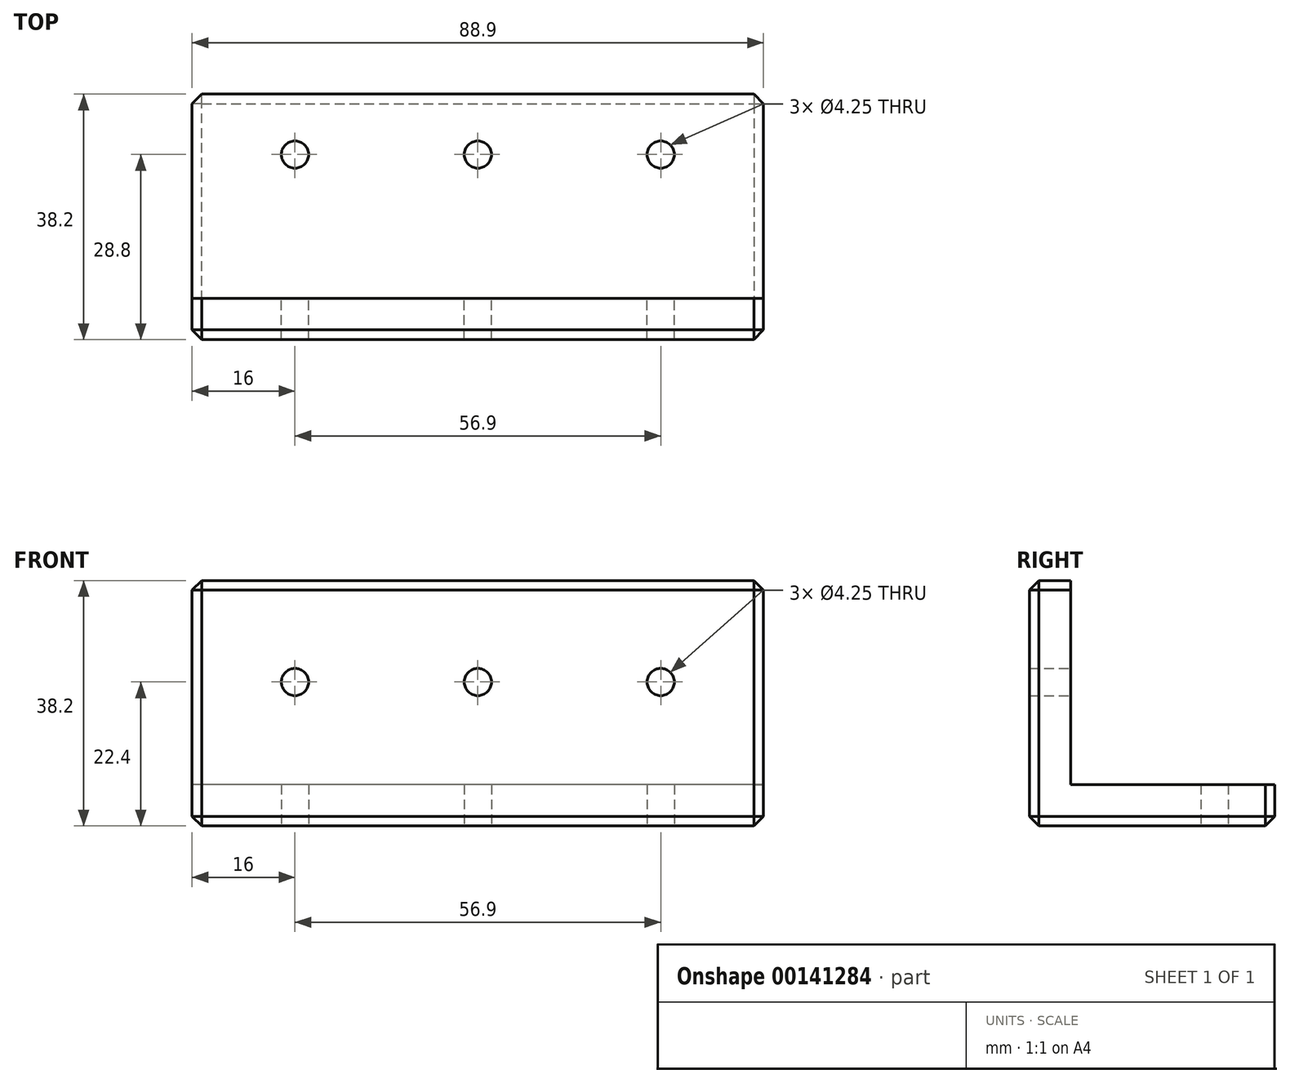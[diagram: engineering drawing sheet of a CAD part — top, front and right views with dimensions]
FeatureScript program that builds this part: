
annotation { "Feature Type Name" : "Feature", "Feature Type Description" : "" }
export const myFeature = defineFeature(function(context is Context, id is Id, definition is map)
    precondition{}
    {
        {
            var Q0;
            Q0=qCreatedBy(makeId("Top.planeOp"),FACE);
            var sketch = newSketch(context, id + "F0", { "sketchPlane" : qUnion([Q0])});
            skLineSegment(sketch, "E0.bottom", {"start": v(44.45, -15.9) * mm, "end": v(-44.45, -15.9) * mm});
            skLineSegment(sketch, "E0.top", {"start": v(44.45, 15.9) * mm, "end": v(-44.45, 15.9) * mm});
            skLineSegment(sketch, "E0.left", {"start": v(44.45, -15.9) * mm, "end": v(44.45, 15.9) * mm});
            skLineSegment(sketch, "E0.right", {"start": v(-44.45, -15.9) * mm, "end": v(-44.45, 15.9) * mm});
            skPoint(sketch, "E0.middle", {"position": v(0, 0) * mm});
            skLineSegment(sketch, "E1", {"start": v(-44.45, -9.5) * mm, "end": v(44.45, -9.5) * mm, "construction": true});
            skCircle(sketch, "E2", {"center": v(0, 6.5) * mm, "radius": 2.12 * mm});
            skCircle(sketch, "E3", {"center": v(-28.45, 6.5) * mm, "radius": 2.12 * mm});
            skCircle(sketch, "E4.MirrorC", {"center": v(28.45, 6.5) * mm, "radius": 2.12 * mm});
            skSolve(sketch);
        }
        {
            var Q0;
            Q0=qSketchRegion(id+"F0",true);
            extrude(context, id + "F1", {"entities" : qUnion([Q0]), "depth" : 6.4 * mm});
        }
        {
            var Q0;
            Q0=makeQuery(id+"F1.opExtrude","SWEPT_FACE",FACE,{"disambiguationData":[OSD([sQuery(id+"F0.wireOp",EDGE,"E0.bottom")])]});
            var sketch = newSketch(context, id + "F2", { "sketchPlane" : qUnion([Q0])});
            skLineSegment(sketch, "E5.bottom", {"start": v(-44.45, 38.2) * mm, "end": v(44.45, 38.2) * mm});
            skLineSegment(sketch, "E5.top", {"start": v(-44.45, 0) * mm, "end": v(44.45, 0) * mm});
            skLineSegment(sketch, "E5.left", {"start": v(-44.45, 38.2) * mm, "end": v(-44.45, 0) * mm});
            skLineSegment(sketch, "E5.right", {"start": v(44.45, 38.2) * mm, "end": v(44.45, 0) * mm});
            skCircle(sketch, "E6", {"center": v(0, 22.4) * mm, "radius": 2.12 * mm});
            skCircle(sketch, "E7", {"center": v(-28.45, 22.4) * mm, "radius": 2.12 * mm});
            skCircle(sketch, "E8.MirrorC", {"center": v(28.45, 22.4) * mm, "radius": 2.12 * mm});
            skSolve(sketch);
        }
        {
            var Q0;
            Q0=qSketchRegion(id+"F2",true);
            extrude(context, id + "F3", {"entities" : qUnion([Q0]), "operationType" : NewBodyOperationType.ADD, "depth" : 6.4 * mm});
        }
        {
            var Q0;
            Q0=makeQuery(id+"F3.opExtrude","CAP_EDGE",EDGE,{"disambiguationData":[OSD([sQuery(id+"F2.wireOp",EDGE,"E5.bottom")])],"isStart":false});
            var Q1;
            Q1=makeQuery(id+"F3.opExtrude","CAP_EDGE",EDGE,{"disambiguationData":[OSD([sQuery(id+"F2.wireOp",EDGE,"E5.top")])],"isStart":false});
            var Q2;
            Q2=makeQuery(id+"F1.opExtrude","CAP_EDGE",EDGE,{"disambiguationData":[OSD([sQuery(id+"F0.wireOp",EDGE,"E0.top")])],"isStart":true});
            var Q3;
            Q3=makeQuery(id+"F3.boolean.opBoolean","MERGE",EDGE,{"derivedFrom":[makeQuery(id+"F1.opExtrude","CAP_EDGE",EDGE,{"disambiguationData":[OSD([sQuery(id+"F0.wireOp",EDGE,"E0.left")])],"isStart":true}),makeQuery(id+"F3.opExtrude","SWEPT_EDGE",EDGE,{"disambiguationData":[OSD([sQuery(id+"F2.wireOp",EDGE,"E5.top"),sQuery(id+"F2.wireOp",EDGE,"E5.right")])]})]});
            var Q4;
            Q4=makeQuery(id+"F1.opExtrude","SWEPT_EDGE",EDGE,{"disambiguationData":[OSD([sQuery(id+"F0.wireOp",EDGE,"E0.top"),sQuery(id+"F0.wireOp",EDGE,"E0.left")])]});
            var Q5;
            Q5=makeQuery(id+"F1.opExtrude","SWEPT_EDGE",EDGE,{"disambiguationData":[OSD([sQuery(id+"F0.wireOp",EDGE,"E0.top"),sQuery(id+"F0.wireOp",EDGE,"E0.right")])]});
            var Q6;
            Q6=makeQuery(id+"F3.boolean.opBoolean","MERGE",EDGE,{"derivedFrom":[makeQuery(id+"F1.opExtrude","CAP_EDGE",EDGE,{"disambiguationData":[OSD([sQuery(id+"F0.wireOp",EDGE,"E0.right")])],"isStart":true}),makeQuery(id+"F3.opExtrude","SWEPT_EDGE",EDGE,{"disambiguationData":[OSD([sQuery(id+"F2.wireOp",EDGE,"E5.top"),sQuery(id+"F2.wireOp",EDGE,"E5.left")])]})]});
            var Q7;
            Q7=makeQuery(id+"F3.opExtrude","CAP_EDGE",EDGE,{"disambiguationData":[OSD([sQuery(id+"F2.wireOp",EDGE,"E5.left")])],"isStart":false});
            var Q8;
            Q8=makeQuery(id+"F3.opExtrude","CAP_EDGE",EDGE,{"disambiguationData":[OSD([sQuery(id+"F2.wireOp",EDGE,"E5.right")])],"isStart":false});
            var Q9;
            Q9=makeQuery(id+"F3.opExtrude","SWEPT_EDGE",EDGE,{"disambiguationData":[OSD([sQuery(id+"F2.wireOp",EDGE,"E5.bottom"),sQuery(id+"F2.wireOp",EDGE,"E5.left")])]});
            var Q10;
            Q10=makeQuery(id+"F3.opExtrude","SWEPT_EDGE",EDGE,{"disambiguationData":[OSD([sQuery(id+"F2.wireOp",EDGE,"E5.bottom"),sQuery(id+"F2.wireOp",EDGE,"E5.right")])]});
            chamfer(context, id + "F4", {"entities" : qUnion([Q0, Q1, Q2, Q3, Q4, Q5, Q6, Q7, Q8, Q9, Q10]), "width" : 1.5 * mm, "tangentPropagation" : true});
        }
    });
